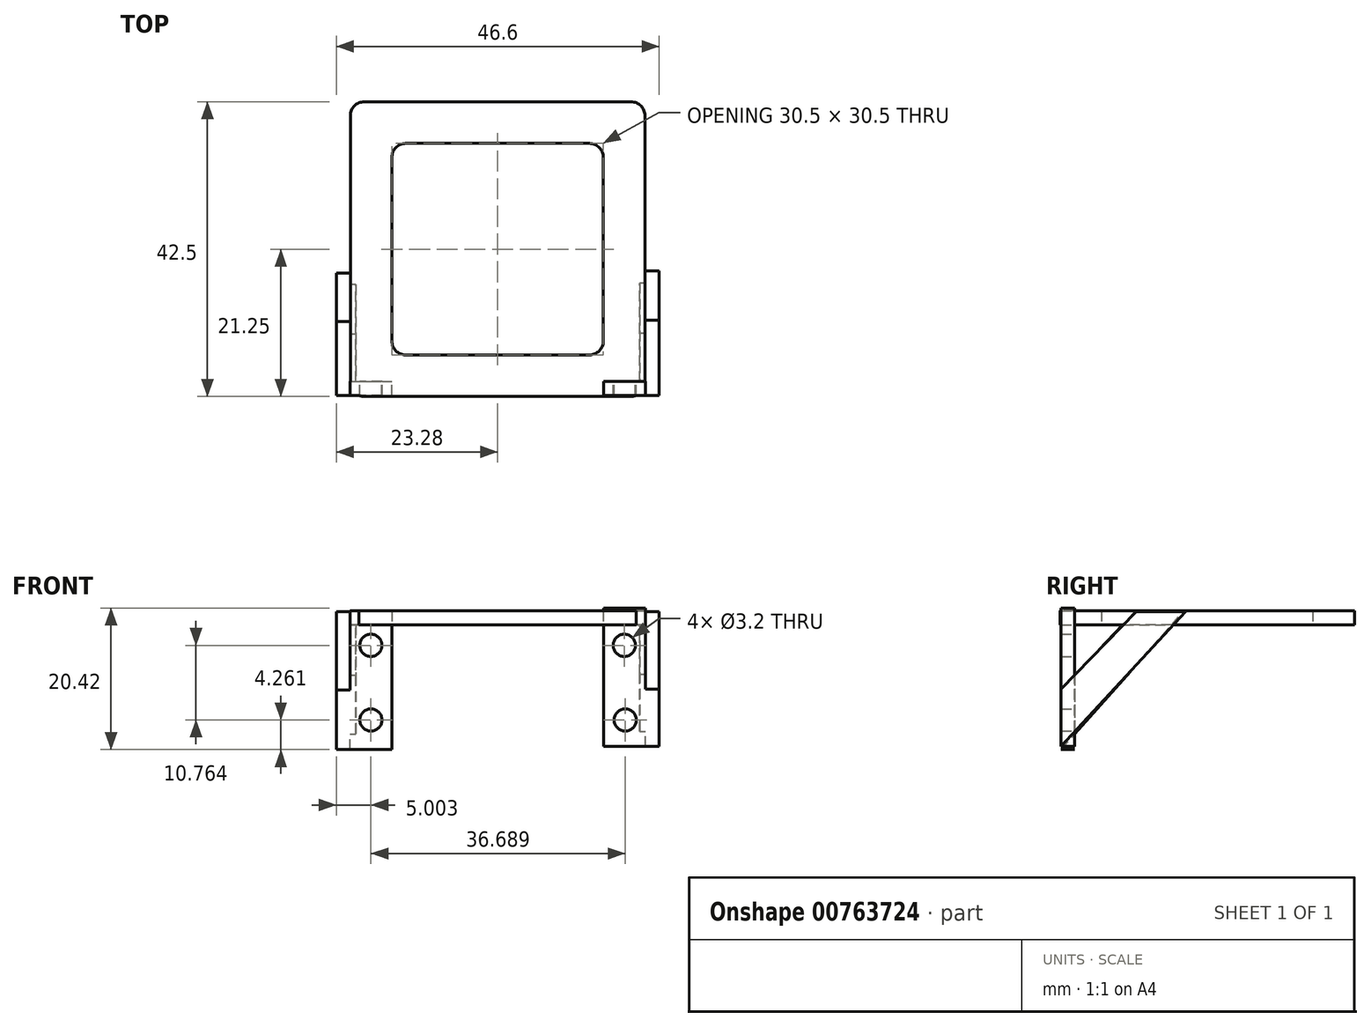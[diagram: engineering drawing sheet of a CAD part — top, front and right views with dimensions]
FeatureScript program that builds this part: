
annotation { "Feature Type Name" : "Feature", "Feature Type Description" : "" }
export const myFeature = defineFeature(function(context is Context, id is Id, definition is map)
    precondition{}
    {
        {
            var Q0;
            Q0=qCreatedBy(makeId("Top.planeOp"),FACE);
            var sketch = newSketch(context, id + "F0", { "sketchPlane" : qUnion([Q0])});
            skLineSegment(sketch, "E0.bottom", {"start": v(13.25, -15.25) * mm, "end": v(-13.25, -15.25) * mm});
            skLineSegment(sketch, "E0.top", {"start": v(13.25, 15.25) * mm, "end": v(-13.25, 15.25) * mm});
            skLineSegment(sketch, "E0.left", {"start": v(15.25, -13.25) * mm, "end": v(15.25, 13.25) * mm});
            skLineSegment(sketch, "E0.right", {"start": v(-15.25, -13.25) * mm, "end": v(-15.25, 13.25) * mm});
            skPoint(sketch, "E0.middle", {"position": v(0, 0) * mm});
            skLineSegment(sketch, "E1.bottom", {"start": v(-19.25, 21.25) * mm, "end": v(19.25, 21.25) * mm});
            skLineSegment(sketch, "E1.top", {"start": v(-19.25, -21.25) * mm, "end": v(19.25, -21.25) * mm});
            skLineSegment(sketch, "E1.left", {"start": v(-21.25, 19.25) * mm, "end": v(-21.25, -19.25) * mm});
            skLineSegment(sketch, "E1.right", {"start": v(21.25, 19.25) * mm, "end": v(21.25, -19.25) * mm});
            skPoint(sketch, "E2.visualSharp", {"position": v(21.25, -21.25) * mm});
            skArc(sketch, "E2.filletArc", {"start": v(19.25, -21.25) * mm, "mid": v(20.66, -20.66) * mm, "end": v(21.25, -19.25) * mm});
            skPoint(sketch, "E3.visualSharp", {"position": v(-21.25, -21.25) * mm});
            skArc(sketch, "E3.filletArc", {"start": v(-21.25, -19.25) * mm, "mid": v(-20.66, -20.66) * mm, "end": v(-19.25, -21.25) * mm});
            skPoint(sketch, "E4.visualSharp", {"position": v(-21.25, 21.25) * mm});
            skArc(sketch, "E4.filletArc", {"start": v(-19.25, 21.25) * mm, "mid": v(-20.66, 20.66) * mm, "end": v(-21.25, 19.25) * mm});
            skPoint(sketch, "E5.visualSharp", {"position": v(21.25, 21.25) * mm});
            skArc(sketch, "E5.filletArc", {"start": v(21.25, 19.25) * mm, "mid": v(20.66, 20.66) * mm, "end": v(19.25, 21.25) * mm});
            skPoint(sketch, "E6.visualSharp", {"position": v(15.25, 15.25) * mm});
            skArc(sketch, "E6.filletArc", {"start": v(15.25, 13.25) * mm, "mid": v(14.66, 14.66) * mm, "end": v(13.25, 15.25) * mm});
            skPoint(sketch, "E7.visualSharp", {"position": v(-15.25, 15.25) * mm});
            skArc(sketch, "E7.filletArc", {"start": v(-13.25, 15.25) * mm, "mid": v(-14.66, 14.66) * mm, "end": v(-15.25, 13.25) * mm});
            skPoint(sketch, "E8.visualSharp", {"position": v(-15.25, -15.25) * mm});
            skArc(sketch, "E8.filletArc", {"start": v(-15.25, -13.25) * mm, "mid": v(-14.66, -14.66) * mm, "end": v(-13.25, -15.25) * mm});
            skPoint(sketch, "E9.visualSharp", {"position": v(15.25, -15.25) * mm});
            skArc(sketch, "E9.filletArc", {"start": v(13.25, -15.25) * mm, "mid": v(14.66, -14.66) * mm, "end": v(15.25, -13.25) * mm});
            skSolve(sketch);
        }
        {
            var Q0;
            Q0=makeQuery(id+"F0.imprint","IMPRINT",FACE,{"disambiguationData":[TD([[makeQuery(id+"F0.imprint","IMPRINT",EDGE,{"derivedFrom":sQuery(id+"F0.wireOp",EDGE,"E0.bottom")}),1.0]])]});
            extrude(context, id + "F1", {"entities" : qUnion([Q0]), "depth" : 2 * mm, "offsetDistance" : 25 * mm});
        }
        {
            var Q0;
            Q0=qCreatedBy(makeId("Front.planeOp"),FACE);
            var sketch = newSketch(context, id + "F2", { "sketchPlane" : qUnion([Q0])});
            skLineSegment(sketch, "E10.bottom", {"start": v(-21.28, 2) * mm, "end": v(-15.28, 2) * mm});
            skLineSegment(sketch, "E10.top", {"start": v(-21.28, -18) * mm, "end": v(-15.28, -18) * mm});
            skLineSegment(sketch, "E10.left", {"start": v(-21.28, 2) * mm, "end": v(-21.28, -18) * mm});
            skLineSegment(sketch, "E10.right", {"start": v(-15.28, 2) * mm, "end": v(-15.28, -18) * mm});
            skLineSegment(sketch, "E11.bottom", {"start": v(21.32, 2.42) * mm, "end": v(15.32, 2.42) * mm});
            skLineSegment(sketch, "E11.top", {"start": v(21.32, -17.58) * mm, "end": v(15.32, -17.58) * mm});
            skLineSegment(sketch, "E11.left", {"start": v(21.32, 2.42) * mm, "end": v(21.32, -17.58) * mm});
            skLineSegment(sketch, "E11.right", {"start": v(15.32, 2.42) * mm, "end": v(15.32, -17.58) * mm});
            skCircle(sketch, "E12", {"center": v(-18.28, -2.97) * mm, "radius": 1.6 * mm});
            skPoint(sketch, "E12.centerSnap0", {"position": v(-18.28, 2) * mm});
            skCircle(sketch, "E13", {"center": v(-18.27, -13.74) * mm, "radius": 1.6 * mm});
            skCircle(sketch, "E14", {"center": v(18.41, -13.74) * mm, "radius": 1.6 * mm});
            skCircle(sketch, "E15", {"center": v(18.27, -2.97) * mm, "radius": 1.6 * mm});
            skSolve(sketch);
        }
        {
            var Q0;
            Q0=makeQuery(id+"F2.imprint","IMPRINT",FACE,{"disambiguationData":[TD([[makeQuery(id+"F2.imprint","IMPRINT",EDGE,{"derivedFrom":sQuery(id+"F2.wireOp",EDGE,"E10.bottom")}),-1.0]])]});
            var Q1;
            Q1=makeQuery(id+"F2.imprint","IMPRINT",FACE,{"disambiguationData":[TD([[makeQuery(id+"F2.imprint","IMPRINT",EDGE,{"derivedFrom":sQuery(id+"F2.wireOp",EDGE,"E11.bottom")}),1.0]])]});
            extrude(context, id + "F3", {"entities" : qUnion([Q0, Q1]), "operationType" : NewBodyOperationType.ADD, "depth" : 21.1 * mm, "offsetDistance" : 25 * mm, "hasSecondDirection" : true, "secondDirectionOppositeDirection" : false, "secondDirectionDepth" : 19.1 * mm});
        }
        {
            var Q0;
            Q0=makeQuery(id+"F3.opExtrude","SWEPT_FACE",FACE,{"disambiguationData":[OSD([sQuery(id+"F2.wireOp",EDGE,"E10.left")])]});
            var sketch = newSketch(context, id + "F4", { "sketchPlane" : qUnion([Q0])});
            skLineSegment(sketch, "E16", {"start": v(21.1, -18) * mm, "end": v(3.42, 1.91) * mm});
            skLineSegment(sketch, "E17", {"start": v(3.42, 1.91) * mm, "end": v(10.41, 1.91) * mm});
            skLineSegment(sketch, "E18", {"start": v(10.41, 1.91) * mm, "end": v(21.1, -9.43) * mm});
            skSolve(sketch);
        }
        {
            var Q0;
            Q0=makeQuery(id+"F3.opExtrude","SWEPT_FACE",FACE,{"disambiguationData":[OSD([sQuery(id+"F2.wireOp",EDGE,"E11.left")])]});
            var sketch = newSketch(context, id + "F5", { "sketchPlane" : qUnion([Q0])});
            skLineSegment(sketch, "E19", {"start": v(-21.1, -9.27) * mm, "end": v(-10.27, 1.91) * mm});
            skLineSegment(sketch, "E20", {"start": v(-10.27, 1.91) * mm, "end": v(-3.12, 1.91) * mm});
            skLineSegment(sketch, "E21", {"start": v(-3.12, 1.91) * mm, "end": v(-21.1, -17.58) * mm});
            skSolve(sketch);
        }
        {
            var Q0;
            {var subQ0=sQuery(id+"F5.wireOp",EDGE,"E20");Q0=makeQuery(id+"F5.imprint","IMPRINT",FACE,{"disambiguationData":[TD([[makeQuery(id+"F5.imprint","IMPRINT",EDGE,{"derivedFrom":subQ0}),-1.0]])]});}
            var Q1;
            {var subQ0=sQuery(id+"F5.wireOp",EDGE,"E19");var subQ1=sQuery(id+"F2.wireOp",EDGE,"E11.left");var subQ2=makeQuery(id+"F3.opExtrude","CAP_EDGE",EDGE,{"disambiguationData":[OSD([subQ1])],"isStart":false});var subQ3=makeQuery(id+"F5.imprint","INTERSECT",VERTEX,{"derivedFrom":[subQ2,subQ0]});Q1=makeQuery(id+"F5.imprint","IMPRINT",FACE,{"disambiguationData":[TD([[makeQuery(id+"F5.imprint","IMPRINT",EDGE,{"disambiguationData":[TD([[subQ3,-1.0]])],"derivedFrom":subQ0}),-1.0]])]});}
            extrude(context, id + "F6", {"entities" : qUnion([Q0, Q1]), "operationType" : NewBodyOperationType.ADD, "depth" : 2 * mm, "offsetDistance" : 25 * mm, "hasSecondDirection" : true, "secondDirectionOppositeDirection" : true, "secondDirectionDepth" : 0.8 * mm});
        }
        {
            var Q0;
            {var subQ0=sQuery(id+"F4.wireOp",EDGE,"E17");Q0=makeQuery(id+"F4.imprint","IMPRINT",FACE,{"disambiguationData":[TD([[makeQuery(id+"F4.imprint","IMPRINT",EDGE,{"derivedFrom":subQ0}),-1.0]])]});}
            var Q1;
            {var subQ1=sQuery(id+"F2.wireOp",EDGE,"E10.left");var subQ2=makeQuery(id+"F3.opExtrude","CAP_EDGE",EDGE,{"disambiguationData":[OSD([subQ1])],"isStart":false});var subQ6=sQuery(id+"F4.wireOp",EDGE,"E18");var subQ7=makeQuery(id+"F4.imprint","INTERSECT",VERTEX,{"derivedFrom":[subQ2,subQ6]});Q1=makeQuery(id+"F4.imprint","IMPRINT",FACE,{"disambiguationData":[TD([[makeQuery(id+"F4.imprint","IMPRINT",EDGE,{"disambiguationData":[TD([[subQ7,1.0]])],"derivedFrom":subQ6}),-1.0]])]});}
            extrude(context, id + "F7", {"entities" : qUnion([Q0, Q1]), "operationType" : NewBodyOperationType.ADD, "depth" : 2 * mm, "offsetDistance" : 25 * mm, "hasSecondDirection" : true, "secondDirectionOppositeDirection" : true, "secondDirectionDepth" : .8 * mm});
        }
    });
